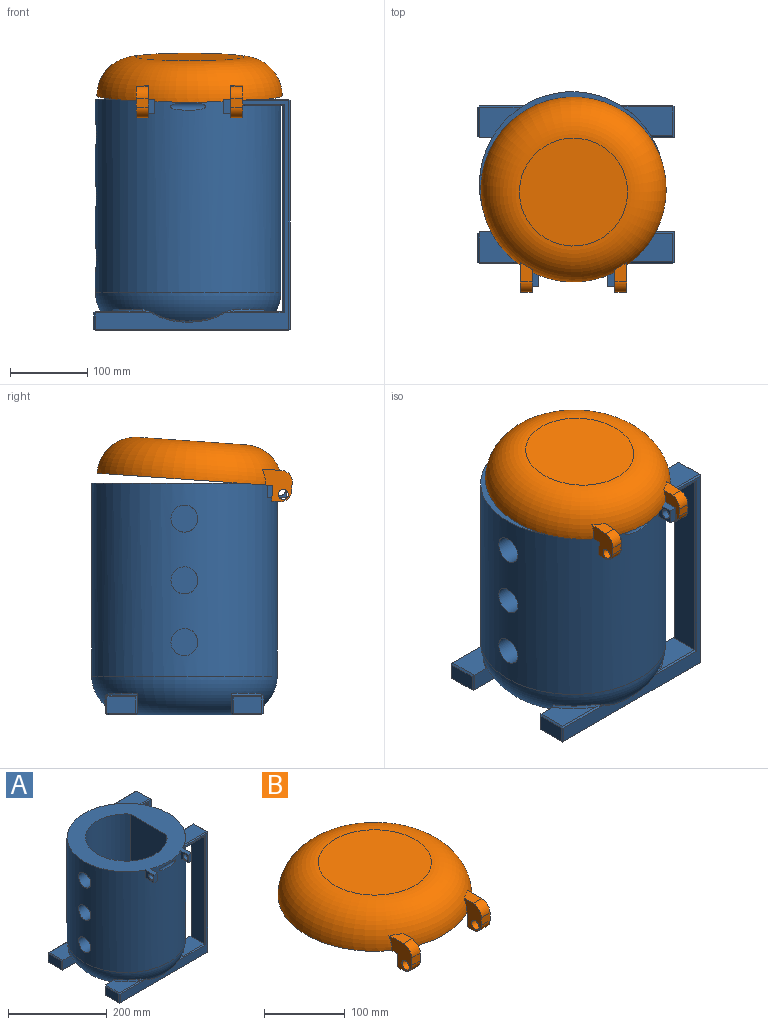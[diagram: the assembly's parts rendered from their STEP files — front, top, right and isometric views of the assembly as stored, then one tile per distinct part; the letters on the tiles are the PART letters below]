
ASSEMBLY  parts=2 mates=1
PART A: 101 faces, bbox 262.6x262.8x300.4 mm
  f0: cylinder r=120.09mm len=250mm, axis (0,0,-1), area 184047.9mm2, adj f3,f4,f8,f9,f17,f18,f23,f25
  f1: cylinder r=82.64mm len=268mm, axis (0,0,1), area 105915.3mm2, adj f4,f6,f30,f31,f32,f33
  f2: plane 266.73x37.33mm, normal (-1,0,0), area 9955.9mm2, adj f21,f29,f80,f86
  f3: torus R=70.09mm, axis (0,0,1), area 36742.7mm2, adj f0,f5,f9,f10,f11,f16,f17,f20
  f4: plane 252.54x240.18mm, normal (0,0,1), area 25643.3mm2, adj f0,f1,f33,f90,f91,f93,f94,f95
  f5: plane 140.18x140.18mm, normal (0,0,-1), area 15434mm2, adj f3
  f6: plane 165.28x146.65mm, normal (0,0,1), area 20125mm2, adj f1,f33
  f7: plane 64.83x39.33mm, normal (0,0,1), area 1558.3mm2, adj f9,f27,f52,f53,f89
  f8: plane 296.29x250.92mm, normal (0,1,0), area 6365.6mm2, adj f0,f36,f40,f45,f46,f49,f51,f52
  f9: plane 295.96x74.56mm, normal (0,-1,0), area 3427.2mm2, adj f0,f3,f7,f26,f34,f37,f53,f88
  f10: cylinder r=80mm len=100.78mm, axis (0,0,-1), area 106.6mm2, adj f3,f14,f37,f41
  f11: plane 62.56x25.92mm, normal (0,-1,0), area 880.6mm2, adj f3,f13,f41,f47,f59
  f12: plane 37.33x21mm, normal (-1,0,0), area 783.8mm2, adj f44,f47,f50,f51
  f13: plane 60.83x39.33mm, normal (0,0,1), area 1477.6mm2, adj f11,f50,f56,f59
  f14: plane 250.57x37.33mm, normal (0,0,-1), area 8221.3mm2, adj f10,f37,f39,f41,f44,f45
  f15: plane 60.83x39.33mm, normal (0,0,1), area 1477.6mm2, adj f20,f75,f78,f79
  f16: cylinder r=80mm len=100.78mm, axis (0,0,-1), area 106.6mm2, adj f3,f22,f64,f68
  f17: plane 295.96x74.56mm, normal (0,1,0), area 3428mm2, adj f0,f3,f21,f24,f60,f64,f85,f86
  f18: plane 296.29x250.92mm, normal (0,-1,0), area 6367.8mm2, adj f0,f61,f65,f69,f74,f77,f78,f80
  f19: plane 37.33x21mm, normal (-1,0,0), area 783.8mm2, adj f70,f73,f74,f75
  f20: plane 62.56x25.92mm, normal (0,1,0), area 880.6mm2, adj f3,f15,f68,f73,f79
  f21: plane 64.83x39.33mm, normal (0,0,1), area 1558.3mm2, adj f2,f17,f82,f85,f86
  f22: plane 250.57x37.33mm, normal (0,0,-1), area 8221.3mm2, adj f16,f64,f66,f68,f69,f70
  f23: plane 64.47x37.33mm, normal (0,0,1), area 1628.5mm2, adj f0,f60,f61,f62
  f24: plane 295.93x39.33mm, normal (1,0,0), area 11637.7mm2, adj f17,f62,f65,f66
  f25: plane 64.47x37.33mm, normal (0,0,1), area 1628.5mm2, adj f0,f34,f35,f36
  f26: plane 295.93x39.33mm, normal (1,0,0), area 11637.7mm2, adj f9,f35,f39,f40
  f27: plane 266.77x37.33mm, normal (-1,0,0), area 9957.2mm2, adj f7,f28,f49,f89
  f28: plane 56.47x37.33mm, normal (0,0,-1), area 1329.9mm2, adj f0,f27,f46,f88
  f29: plane 56.47x37.33mm, normal (0,0,-1), area 1329.9mm2, adj f0,f2,f77,f87
  f30: cylinder r=17.5mm len=39.32mm, axis (1,0,0), area 4150.1mm2, adj f0,f1
  f31: cylinder r=17.5mm len=39.32mm, axis (1,0,0), area 4150.1mm2, adj f0,f1
  f32: cylinder r=17.5mm len=39.32mm, axis (1,0,0), area 4150.1mm2, adj f0,f1
  f33: plane 268x104.54mm, normal (-1,0,0), area 28015.9mm2, adj f1,f4,f6
  f34: plane 30.13x2.01mm, normal (0,-0.71,0.71), area 80.6mm2, adj f0,f9,f25,f35
  f35: plane 39.33x2mm, normal (0.71,0,0.71), area 108.4mm2, adj f25,f26,f34,f38
  f36: plane 67.65x2.02mm, normal (0,0.71,0.71), area 186.8mm2, adj f0,f8,f25,f38
  f37: plane 83.26x2.12mm, normal (0,-0.71,-0.71), area 224.1mm2, adj f3,f9,f10,f14,f39
  f38: plane 2x2mm, normal (0.58,0.58,0.58), area 3.5mm2, adj f35,f36,f40
  f39: plane 39.33x2mm, normal (0.71,0,-0.71), area 108.4mm2, adj f14,f26,f37,f42
  f40: plane 295.93x2mm, normal (0.71,0.71,0), area 837mm2, adj f8,f26,f38,f42
  f41: plane 71.26x2.12mm, normal (0,-0.71,-0.71), area 193mm2, adj f3,f10,f11,f14,f43
  f42: plane 2x2mm, normal (0.58,0.58,-0.58), area 3.5mm2, adj f39,f40,f45
  f43: plane 2x2mm, normal (-0.58,-0.58,-0.58), area 3.5mm2, adj f41,f44,f47
  f44: plane 37.33x2mm, normal (-0.71,0,-0.71), area 105.6mm2, adj f12,f14,f43,f48
  f45: plane 250.57x2mm, normal (0,0.71,-0.71), area 708.7mm2, adj f8,f14,f42,f48
  f46: plane 61.65x2.02mm, normal (0,0.71,-0.71), area 167mm2, adj f0,f8,f28,f49
  f47: plane 23x2mm, normal (-0.71,-0.71,0), area 62.2mm2, adj f11,f12,f43,f50
  f48: plane 2x2mm, normal (-0.58,0.58,-0.58), area 3.5mm2, adj f44,f45,f51
  f49: plane 270.77x2mm, normal (-0.71,0.71,0), area 760.2mm2, adj f8,f27,f46,f52
  f50: plane 39.33x2mm, normal (-0.71,0,0.71), area 108.4mm2, adj f12,f13,f47,f54
  f51: plane 21x2mm, normal (-0.71,0.71,0), area 59.4mm2, adj f8,f12,f48,f54
  f52: plane 77.3x2mm, normal (0,0.71,0.71), area 198.2mm2, adj f7,f8,f49,f55
  f53: cone r=114.93mm half-angle=31.9deg, axis (0,0,-1), area 189mm2, adj f3,f7,f9,f55
  f54: plane 2x2mm, normal (-0.58,0.58,0.58), area 3.5mm2, adj f50,f51,f56
  f55: bspline ~13.18x4.91mm, area 29mm2, adj f3,f52,f53,f57
  f56: plane 73.3x2mm, normal (0,0.71,0.71), area 189.7mm2, adj f8,f13,f54,f58
  f57: bspline ~93.96x13.06mm, area 149.7mm2, adj f3,f8,f55,f58
  f58: bspline ~13.17x4.88mm, area 29mm2, adj f3,f56,f57,f59
  f59: cone r=114.93mm half-angle=31.9deg, axis (0,0,-1), area 189mm2, adj f3,f11,f13,f58
  f60: plane 30.13x2.01mm, normal (0,0.71,0.71), area 80.6mm2, adj f0,f17,f23,f62
  f61: plane 67.65x2.02mm, normal (0,-0.71,0.71), area 186.8mm2, adj f0,f18,f23,f63
  f62: plane 39.33x2mm, normal (0.71,0,0.71), area 108.4mm2, adj f23,f24,f60,f63
  f63: plane 2x2mm, normal (0.58,-0.58,0.58), area 3.5mm2, adj f61,f62,f65
  f64: plane 83.26x2.12mm, normal (0,0.71,-0.71), area 224.1mm2, adj f3,f16,f17,f22,f66
  f65: plane 295.93x2mm, normal (0.71,-0.71,0), area 837mm2, adj f18,f24,f63,f67
  f66: plane 39.33x2mm, normal (0.71,0,-0.71), area 108.4mm2, adj f22,f24,f64,f67
  f67: plane 2x2mm, normal (0.58,-0.58,-0.58), area 3.5mm2, adj f65,f66,f69
  f68: plane 71.26x2.12mm, normal (0,0.71,-0.71), area 193mm2, adj f3,f16,f20,f22,f71
  f69: plane 250.57x2mm, normal (0,-0.71,-0.71), area 708.7mm2, adj f18,f22,f67,f72
  f70: plane 37.33x2mm, normal (-0.71,0,-0.71), area 105.6mm2, adj f19,f22,f71,f72
  f71: plane 2x2mm, normal (-0.58,0.58,-0.58), area 3.5mm2, adj f68,f70,f73
  f72: plane 2x2mm, normal (-0.58,-0.58,-0.58), area 3.5mm2, adj f69,f70,f74
  f73: plane 23x2mm, normal (-0.71,0.71,0), area 62.2mm2, adj f19,f20,f71,f75
  f74: plane 21x2mm, normal (-0.71,-0.71,0), area 59.4mm2, adj f18,f19,f72,f76
  f75: plane 39.33x2mm, normal (-0.71,0,0.71), area 108.4mm2, adj f15,f19,f73,f76
  f76: plane 2x2mm, normal (-0.58,-0.58,0.58), area 3.5mm2, adj f74,f75,f78
  f77: plane 61.65x2.02mm, normal (0,-0.71,-0.71), area 167mm2, adj f0,f18,f29,f80
  f78: plane 73.3x2mm, normal (0,-0.71,0.71), area 189.7mm2, adj f15,f18,f76,f81
  f79: cone r=114.93mm half-angle=31.9deg, axis (0,0,-1), area 189mm2, adj f3,f15,f20,f81
  f80: plane 270.73x2mm, normal (-0.71,-0.71,0), area 760.1mm2, adj f2,f18,f77,f82
  f81: bspline ~13.18x4.91mm, area 29mm2, adj f3,f78,f79,f83
  f82: plane 77.3x2mm, normal (0,-0.71,0.71), area 198.2mm2, adj f18,f21,f80,f84
  f83: bspline ~93.96x13.06mm, area 149.7mm2, adj f3,f18,f81,f84
  f84: bspline ~13.17x4.88mm, area 29mm2, adj f3,f82,f83,f85
  f85: cone r=114.93mm half-angle=31.9deg, axis (0,0,-1), area 189mm2, adj f3,f17,f21,f84
  f86: plane 268.73x2mm, normal (-0.71,0.71,0), area 757.2mm2, adj f2,f17,f21,f87
  f87: plane 22.13x2.01mm, normal (0,0.71,-0.71), area 58mm2, adj f0,f17,f29,f86
  f88: plane 22.13x2.01mm, normal (0,-0.71,-0.71), area 58mm2, adj f0,f9,f28,f89
  f89: plane 268.77x2mm, normal (-0.71,-0.71,0), area 757.4mm2, adj f7,f9,f27,f88
  f90: plane 24.91x19.11mm, normal (-1,0,0), area 343.3mm2, adj f0,f4,f92,f93,f99
  f91: plane 20.5x19.11mm, normal (1,0,0), area 258.9mm2, adj f0,f4,f92,f93,f99
  f92: plane 24.91x10mm, normal (0,0,-1), area 226.1mm2, adj f0,f90,f91,f93
  f93: plane 19.11x10mm, normal (0,-1,0), area 191.1mm2, adj f4,f90,f91,f92
  f94: plane 21.21x19.11mm, normal (-1,0,0), area 272.6mm2, adj f0,f4,f96,f97,f98
  f95: plane 25.83x19.11mm, normal (1,0,0), area 360.7mm2, adj f0,f4,f96,f97,f98
  f96: plane 25.83x10mm, normal (0,0,-1), area 234.3mm2, adj f0,f94,f95,f97
  f97: plane 19.11x10mm, normal (0,-1,0), area 191.1mm2, adj f4,f94,f95,f96
  f98: cylinder r=6.5mm len=13mm, axis (-1,0,0), area 408.4mm2, adj f94,f95
  f99: cylinder r=6.5mm len=13mm, axis (-1,0,0), area 408.4mm2, adj f90,f91
  f100: cylinder r=6.5mm len=46.13mm, axis (-1,0,0), area 401.1mm2, adj f0
PART B: 21 faces, bbox 260x263x70.2 mm
  f0: plane 15.25x10.33mm, normal (0,0,-1), area 157.5mm2, adj f2,f3,f13,f15
  f1: plane 40.45x30.27mm, normal (1,0,0), area 825.7mm2, adj f4,f5,f8,f9,f10,f14,f17,f18
  f2: plane 40.45x30.27mm, normal (-1,0,0), area 825.7mm2, adj f0,f4,f5,f11,f12,f13,f15,f16
  f3: plane 40.45x39.78mm, normal (1,0,0), area 1011.5mm2, adj f0,f4,f5,f11,f12,f13,f15,f16
  f4: plane 240.18x240.18mm, normal (0,0,-1), area 45457.9mm2, adj f1,f2,f3,f5,f7,f13,f14
  f5: torus R=70.09mm, axis (0,0,1), area 49554.7mm2, adj f1,f2,f3,f4,f6,f7,f8,f11
  f6: plane 140.18x140.18mm, normal (0,0,1), area 15434mm2, adj f5
  f7: plane 40.45x39.78mm, normal (-1,0,0), area 1011.5mm2, adj f4,f5,f8,f9,f10,f14,f17,f18
  f8: plane 25.28x15.25mm, normal (0,0,1), area 308.8mm2, adj f1,f5,f7,f17
  f9: plane 15.25x10.33mm, normal (0,0,-1), area 157.5mm2, adj f1,f7,f14,f18
  f10: plane 15.25x11.47mm, normal (0,-1,0), area 174.9mm2, adj f1,f7,f17,f18
  f11: plane 25.28x15.25mm, normal (0,0,1), area 308.8mm2, adj f2,f3,f5,f16
  f12: plane 15.25x11.47mm, normal (0,-1,0), area 174.9mm2, adj f2,f3,f15,f16
  f13: plane 20.22x15.25mm, normal (0,1,0), area 308.3mm2, adj f0,f2,f3,f4
  f14: plane 20.22x15.25mm, normal (0,1,0), area 308.3mm2, adj f1,f4,f7,f9
  f15: cylinder r=14.49mm len=15.25mm, axis (-1,0,0), area 346.9mm2, adj f0,f2,f3,f12
  f16: cylinder r=14.49mm len=15.25mm, axis (1,0,0), area 346.9mm2, adj f2,f3,f11,f12
  f17: cylinder r=14.49mm len=15.25mm, axis (1,0,0), area 346.9mm2, adj f1,f7,f8,f10
  f18: cylinder r=14.49mm len=15.25mm, axis (-1,0,0), area 346.9mm2, adj f1,f7,f9,f10
  f19: cylinder r=6.5mm len=15.25mm, axis (-1,0,0), area 622.7mm2, adj f1,f7
  f20: cylinder r=6.5mm len=15.25mm, axis (-1,0,0), area 622.7mm2, adj f2,f3
PLACE A t=(189.28,-405.44,-220.31)mm fixed
PLACE B rot(axis=(1,0,0),4deg) t=(191.06,-411.98,84.33)mm
MATE revolute B.f15 <-> A.f98  axis (-1,0,0) through (244.53,-529.8,70.31)mm
